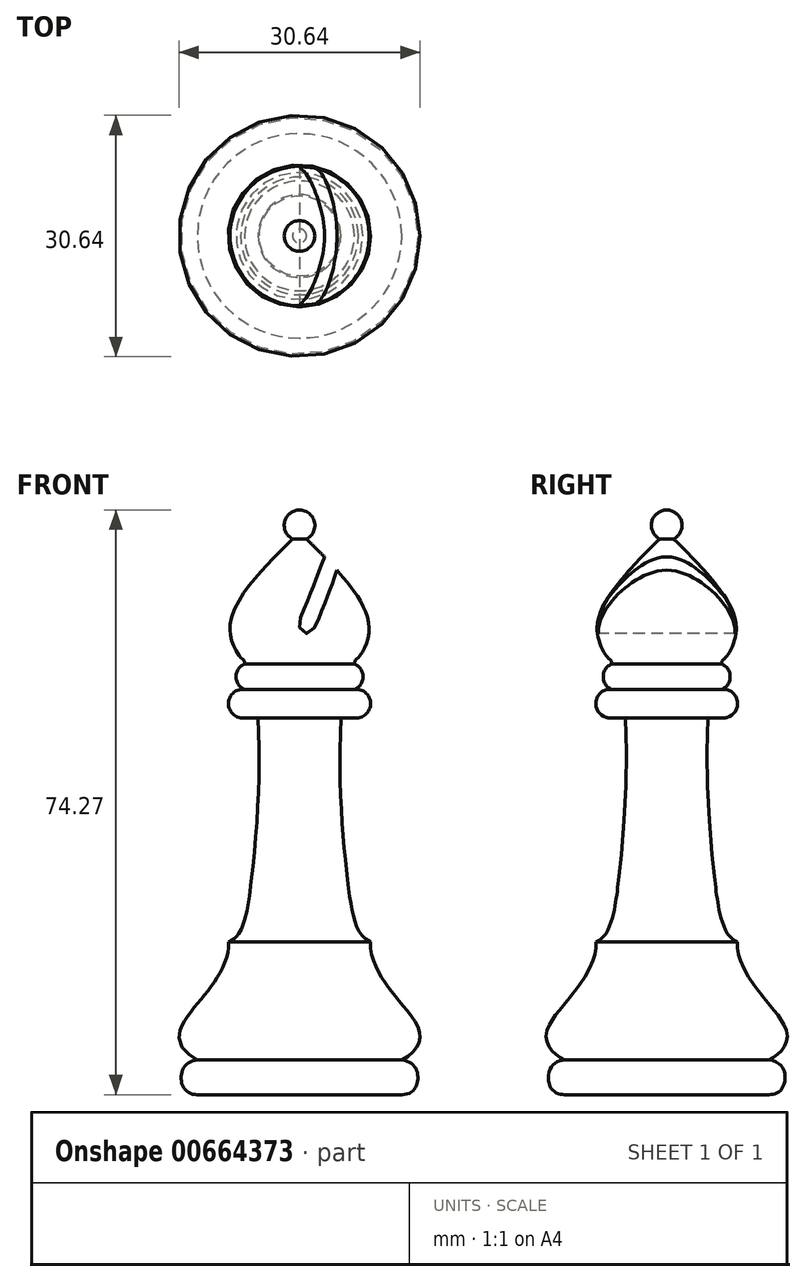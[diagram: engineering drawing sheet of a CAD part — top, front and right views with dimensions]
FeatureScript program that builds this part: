
annotation { "Feature Type Name" : "Feature", "Feature Type Description" : "" }
export const myFeature = defineFeature(function(context is Context, id is Id, definition is map)
    precondition{}
    {
        {
            var Q0;
            Q0=qCreatedBy(makeId("Front.planeOp"),FACE);
            var sketch = newSketch(context, id + "F0", { "sketchPlane" : qUnion([Q0])});
            skLineSegment(sketch, "E0", {"start": v(0, 0) * mm, "end": v(13, 0) * mm});
            skFitSpline(sketch, "E1", {"points": [v(13, 0) * mm, v(15.04, 2.06) * mm, v(12.99, 4.4) * mm], "startDerivative": vector(8.66, 0) * mm, "endDerivative": vector(-8.91, 0.72) * mm});
            skFitSpline(sketch, "E2", {"points": [v(8.99, 19.41) * mm, v(7.12, 21.75) * mm, v(6.12, 27.19) * mm, v(5.26, 47.87) * mm], "startDerivative": vector(-15.43, 6.56) * mm, "endDerivative": vector(2.36, 47.71) * mm});
            skLineSegment(sketch, "E3", {"start": v(0, 74.27) * mm, "end": v(0, 0) * mm});
            skLineSegment(sketch, "E4", {"start": v(5.26, 47.87) * mm, "end": v(7.48, 47.87) * mm});
            skArc(sketch, "E5", {"start": v(7.48, 47.87) * mm, "mid": v(9.02, 49.68) * mm, "end": v(7.48, 51.48) * mm});
            skLineSegment(sketch, "E6", {"start": v(7.48, 51.48) * mm, "end": v(6.97, 51.48) * mm});
            skArc(sketch, "E7", {"start": v(6.97, 51.48) * mm, "mid": v(8.06, 53.1) * mm, "end": v(6.97, 54.7) * mm});
            skFitSpline(sketch, "E8", {"points": [v(6.97, 54.7) * mm, v(7.3, 55.36) * mm, v(8.84, 59.15) * mm, v(5.73, 65.48) * mm, v(0, 71.46) * mm], "startDerivative": vector(1.07, 17.43) * mm, "endDerivative": vector(-25.81, 25.17) * mm});
            skArc(sketch, "E9", {"start": v(0, 70.38) * mm, "mid": v(1.94, 72.33) * mm, "end": v(0, 74.27) * mm});
            skFitSpline(sketch, "E10", {"points": [v(8.99, 19.41) * mm, v(10.43, 14.93) * mm, v(12.99, 11.52) * mm, v(15.32, 7.54) * mm, v(12.99, 4.4) * mm], "startDerivative": vector(-1.1, -18.82) * mm, "endDerivative": vector(-19.73, -10.73) * mm});
            skLineSegment(sketch, "E11", {"start": v(-4.56, 74.27) * mm, "end": v(-4.56, 0) * mm});
            skSolve(sketch);
        }
        {
            var Q0;
            Q0 = qSketchRegion(id + "F0", true);
            var Q1;
            Q1=sQuery(id+"F0.wireOp",EDGE,"E3");
            revolve(context, id + "F1", {"surfaceOperationType" : NewSurfaceOperationType.NEW, "entities" : qUnion([Q0]), "axis" : qUnion([Q1]), "revolveType" : RevolveType.FULL});
        }
        {
            var Q0;
            Q0=qCreatedBy(makeId("Front.planeOp"),FACE);
            cPlane(context, id + "F2", {"entities" : qUnion([Q0]), "cplaneType" : CPlaneType.OFFSET, "offset" : 9.7 * mm, "width" : 150 * mm, "height" : 150 * mm});
        }
        {
            var Q0;
            Q0=qCreatedBy(id+"F2.planeOp",FACE);
            var sketch = newSketch(context, id + "F3", { "sketchPlane" : qUnion([Q0])});
            skLineSegment(sketch, "E12", {"start": v(4.4, 68.41) * mm, "end": v(3.21, 68.41) * mm});
            skFitSpline(sketch, "E13", {"points": [v(3.21, 68.41) * mm, v(1.08, 62.95) * mm, v(0, 59.43) * mm, v(0.69, 58.6) * mm, v(1.48, 58.8) * mm, v(2.88, 61.6) * mm, v(4.78, 66.7) * mm], "startDerivative": vector(-13.38, -34.57) * mm, "endDerivative": vector(12.43, 37.3) * mm});
            skLineSegment(sketch, "E14", {"start": v(3.21, 68.41) * mm, "end": v(4.78, 66.7) * mm});
            skSolve(sketch);
        }
        {
            var Q0;
            Q0 = qSketchRegion(id + "F3", true);
            extrude(context, id + "F4", {"entities" : qUnion([Q0]), "operationType" : NewBodyOperationType.REMOVE, "oppositeDirection" : true, "depth" : 25 * mm, "offsetDistance" : 25 * mm});
        }
    });
